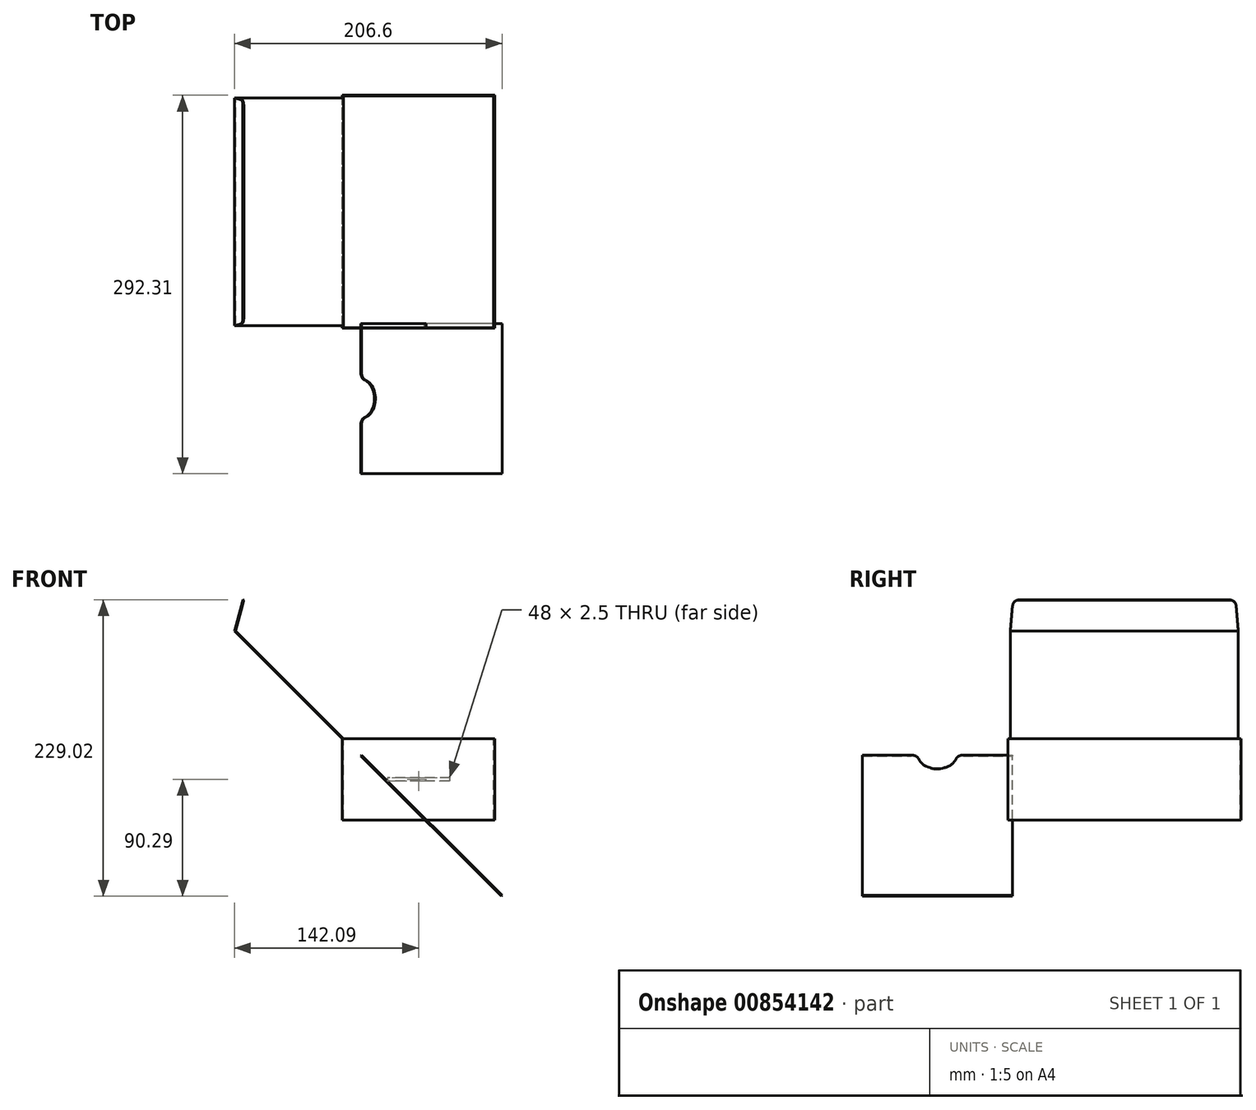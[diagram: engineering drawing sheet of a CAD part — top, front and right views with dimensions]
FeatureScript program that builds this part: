
annotation { "Feature Type Name" : "Feature", "Feature Type Description" : "" }
export const myFeature = defineFeature(function(context is Context, id is Id, definition is map)
    precondition{}
    {
        {
            var Q0;
            Q0=qCreatedBy(makeId("Top.planeOp"),FACE);
            var sketch = newSketch(context, id + "F0", { "sketchPlane" : qUnion([Q0])});
            skLineSegment(sketch, "E0.bottom", {"start": v(59, -90) * mm, "end": v(-59, -90) * mm});
            skLineSegment(sketch, "E0.top", {"start": v(59, 90) * mm, "end": v(-59, 90) * mm});
            skLineSegment(sketch, "E0.left", {"start": v(59, -90) * mm, "end": v(59, 90) * mm});
            skLineSegment(sketch, "E0.right", {"start": v(-59, -90) * mm, "end": v(-59, 90) * mm});
            skPoint(sketch, "E0.middle", {"position": v(0, 0) * mm});
            skSolve(sketch);
        }
        {
            var Q0;
            Q0=makeQuery(id+"F0.imprint","IMPRINT",FACE,{"disambiguationData":[TD([[makeQuery(id+"F0.imprint","IMPRINT",EDGE,{"derivedFrom":sQuery(id+"F0.wireOp",EDGE,"E0.bottom")}),-1.0]])]});
            extrude(context, id + "F1", {"entities" : qUnion([Q0]), "depth" : 63 * mm, "offsetDistance" : 25 * mm});
        }
        {
            var Q0;
            Q0=makeQuery(id+"F1.opExtrude","CAP_FACE",FACE,{"disambiguationData":[OSD([sQuery(id+"F0.wireOp",EDGE,"E0.bottom"),sQuery(id+"F0.wireOp",EDGE,"E0.top"),sQuery(id+"F0.wireOp",EDGE,"E0.left"),sQuery(id+"F0.wireOp",EDGE,"E0.right")])],"isStart":false});
            var sketch = newSketch(context, id + "F2", { "sketchPlane" : qUnion([Q0])});
            skLineSegment(sketch, "E1.bottom", {"start": v(58, -89.5) * mm, "end": v(-58, -89.5) * mm});
            skLineSegment(sketch, "E1.top", {"start": v(58, 89.5) * mm, "end": v(-58, 89.5) * mm});
            skLineSegment(sketch, "E1.left", {"start": v(58, -89.5) * mm, "end": v(58, 89.5) * mm});
            skLineSegment(sketch, "E1.right", {"start": v(-58, -89.5) * mm, "end": v(-58, 89.5) * mm});
            skPoint(sketch, "E1.middle", {"position": v(0, 0) * mm});
            skSolve(sketch);
        }
        {
            var Q0;
            Q0 = qSketchRegion(id + "F2", true);
            extrude(context, id + "F3", {"entities" : qUnion([Q0]), "operationType" : NewBodyOperationType.REMOVE, "oppositeDirection" : true, "depth" : 62.5 * mm, "offsetDistance" : 25 * mm});
        }
        {
            var Q0;
            Q0=qCreatedBy(makeId("Front.planeOp"),FACE);
            var sketch = newSketch(context, id + "F4", { "sketchPlane" : qUnion([Q0])});
            skLineSegment(sketch, "E2", {"start": v(-59, 63) * mm, "end": v(-142.09, 146.09) * mm});
            skLineSegment(sketch, "E3", {"start": v(-142.09, 146.09) * mm, "end": v(-135.61, 170.23) * mm});
            skLineSegment(sketch, "E4", {"start": v(-59, 63) * mm, "end": v(-57.99, 63) * mm});
            skLineSegment(sketch, "E5", {"start": v(-57.99, 63) * mm, "end": v(-141.26, 146.27) * mm});
            skLineSegment(sketch, "E6", {"start": v(-141.26, 146.27) * mm, "end": v(-134.9, 170.04) * mm});
            skLineSegment(sketch, "E7", {"start": v(-135.61, 170.23) * mm, "end": v(-134.9, 170.04) * mm});
            skSolve(sketch);
        }
        {
            var Q0;
            Q0 = qSketchRegion(id + "F4", true);
            extrude(context, id + "F5", {"entities" : qUnion([Q0]), "operationType" : NewBodyOperationType.ADD, "depth" : 88 * mm, "offsetDistance" : 25 * mm, "hasSecondDirection" : true, "secondDirectionOppositeDirection" : true, "secondDirectionDepth" : 88 * mm});
        }
        {
            var Q0;
            Q0=makeQuery(id+"F5.opExtrude","CAP_EDGE",EDGE,{"disambiguationData":[OSD([sQuery(id+"F4.wireOp",EDGE,"E7")])],"isStart":false});
            var Q1;
            Q1=makeQuery(id+"F5.opExtrude","CAP_EDGE",EDGE,{"disambiguationData":[OSD([sQuery(id+"F4.wireOp",EDGE,"E7")])],"isStart":true});
            chamfer(context, id + "F6", {"entities" : qUnion([Q0, Q1]), "chamferType" : ChamferType.OFFSET_ANGLE, "width" : 24 * mm, "oppositeDirection" : true, "angle" : 5 * degree, "tangentPropagation" : true});
        }
        {
            var Q0;
            {var subQ0=sQuery(id+"F4.wireOp",EDGE,"E7");Q0=makeQuery(id+"F6.opChamfer","BLEND_EDGE",EDGE,{"blendedFrom":[makeQuery(id+"F5.opExtrude","CAP_EDGE",EDGE,{"disambiguationData":[OSD([subQ0])],"isStart":true}),makeQuery(id+"F5.opExtrude","SWEPT_FACE",FACE,{"disambiguationData":[OSD([subQ0])]})],"blendedInto":[makeQuery(id+"F5.opExtrude","SWEPT_FACE",FACE,{"disambiguationData":[OSD([subQ0])]})]});}
            var Q1;
            {var subQ0=sQuery(id+"F4.wireOp",EDGE,"E7");Q1=makeQuery(id+"F6.opChamfer","BLEND_EDGE",EDGE,{"blendedFrom":[makeQuery(id+"F5.opExtrude","CAP_EDGE",EDGE,{"disambiguationData":[OSD([subQ0])],"isStart":false}),makeQuery(id+"F5.opExtrude","SWEPT_FACE",FACE,{"disambiguationData":[OSD([subQ0])]})],"blendedInto":[makeQuery(id+"F5.opExtrude","SWEPT_FACE",FACE,{"disambiguationData":[OSD([subQ0])]})]});}
            fillet(context, id + "F7", {"entities" : qUnion([Q0, Q1]), "radius" : 5 * mm, "tangentPropagation" : true, "allowEdgeOverflow" : false});
        }
        {
            var Q0;
            Q0=makeQuery(id+"F1.opExtrude","SWEPT_FACE",FACE,{"disambiguationData":[OSD([sQuery(id+"F0.wireOp",EDGE,"E0.top")])]});
            var sketch = newSketch(context, id + "F8", { "sketchPlane" : qUnion([Q0])});
            skLineSegment(sketch, "E8", {"start": v(0, 0) * mm, "end": v(0, 31.5) * mm, "construction": true});
            skPoint(sketch, "E9.orphan", {"position": v(59, 31.5) * mm});
            skLineSegment(sketch, "E10.bottom", {"start": v(-24, 32.75) * mm, "end": v(24, 32.75) * mm});
            skLineSegment(sketch, "E10.top", {"start": v(-24, 30.25) * mm, "end": v(24, 30.25) * mm});
            skLineSegment(sketch, "E10.left", {"start": v(-24, 32.75) * mm, "end": v(-24, 30.25) * mm});
            skLineSegment(sketch, "E10.right", {"start": v(24, 32.75) * mm, "end": v(24, 30.25) * mm});
            skPoint(sketch, "E10.middle", {"position": v(0, 31.5) * mm});
            skSolve(sketch);
        }
        {
            var Q0;
            Q0 = qSketchRegion(id + "F8", true);
            extrude(context, id + "F9", {"entities" : qUnion([Q0]), "operationType" : NewBodyOperationType.REMOVE, "oppositeDirection" : true, "depth" : 2 * mm, "offsetDistance" : 25 * mm});
        }
        {
            var Q0;
            Q0=makeQuery(id+"F5.opExtrude","SWEPT_FACE",FACE,{"disambiguationData":[OSD([sQuery(id+"F4.wireOp",EDGE,"E5")])]});
            var sketch = newSketch(context, id + "F10", { "sketchPlane" : qUnion([Q0])});
            skLineSegment(sketch, "E11.bottom", {"start": v(-86.55, -86.68) * mm, "end": v(-202.31, -86.68) * mm});
            skLineSegment(sketch, "E11.top", {"start": v(-86.55, 86.68) * mm, "end": v(-202.31, 86.68) * mm, "construction": true});
            skLineSegment(sketch, "E11.left", {"start": v(-86.55, -86.68) * mm, "end": v(-86.55, 66.68) * mm});
            skLineSegment(sketch, "E11.right", {"start": v(-202.31, -86.68) * mm, "end": v(-202.31, 66.68) * mm});
            skPoint(sketch, "E11.middle", {"position": v(-144.43, 0) * mm});
            skPoint(sketch, "E11.middle.positionSnap0", {"position": v(-203.31, 0) * mm});
            skPoint(sketch, "E11.middle.positionSnap1", {"position": v(-144.43, -88) * mm});
            skPoint(sketch, "E11.centerSnap0", {"position": v(-203.31, 0) * mm});
            skPoint(sketch, "E11.centerSnap1", {"position": v(-144.43, -88) * mm});
            skArc(sketch, "E12", {"start": v(-158.8, 62.4) * mm, "mid": v(-144.43, 51.68) * mm, "end": v(-130.06, 62.4) * mm});
            skLineSegment(sketch, "E13", {"start": v(-202.31, 66.68) * mm, "end": v(-164.56, 66.68) * mm});
            skPoint(sketch, "E14.orphan", {"position": v(-243.09, 66.68) * mm});
            skLineSegment(sketch, "E15.trimOffspring", {"start": v(-124.3, 66.68) * mm, "end": v(-86.55, 66.68) * mm});
            skPoint(sketch, "E16.visualSharp", {"position": v(-159.43, 66.68) * mm});
            skArc(sketch, "E16.filletArc", {"start": v(-158.8, 62.4) * mm, "mid": v(-160.97, 65.5) * mm, "end": v(-164.56, 66.68) * mm});
            skPoint(sketch, "E17.visualSharp", {"position": v(-129.43, 66.68) * mm});
            skArc(sketch, "E17.filletArc", {"start": v(-124.3, 66.68) * mm, "mid": v(-127.9, 65.5) * mm, "end": v(-130.06, 62.4) * mm});
            skSolve(sketch);
        }
        {
            var Q0;
            Q0 = qSketchRegion(id + "F10", true);
            extrude(context, id + "F11", {"entities" : qUnion([Q0]), "operationType" : NewBodyOperationType.ADD, "depth" : 1 * mm, "offsetDistance" : 25 * mm});
        }
    });
